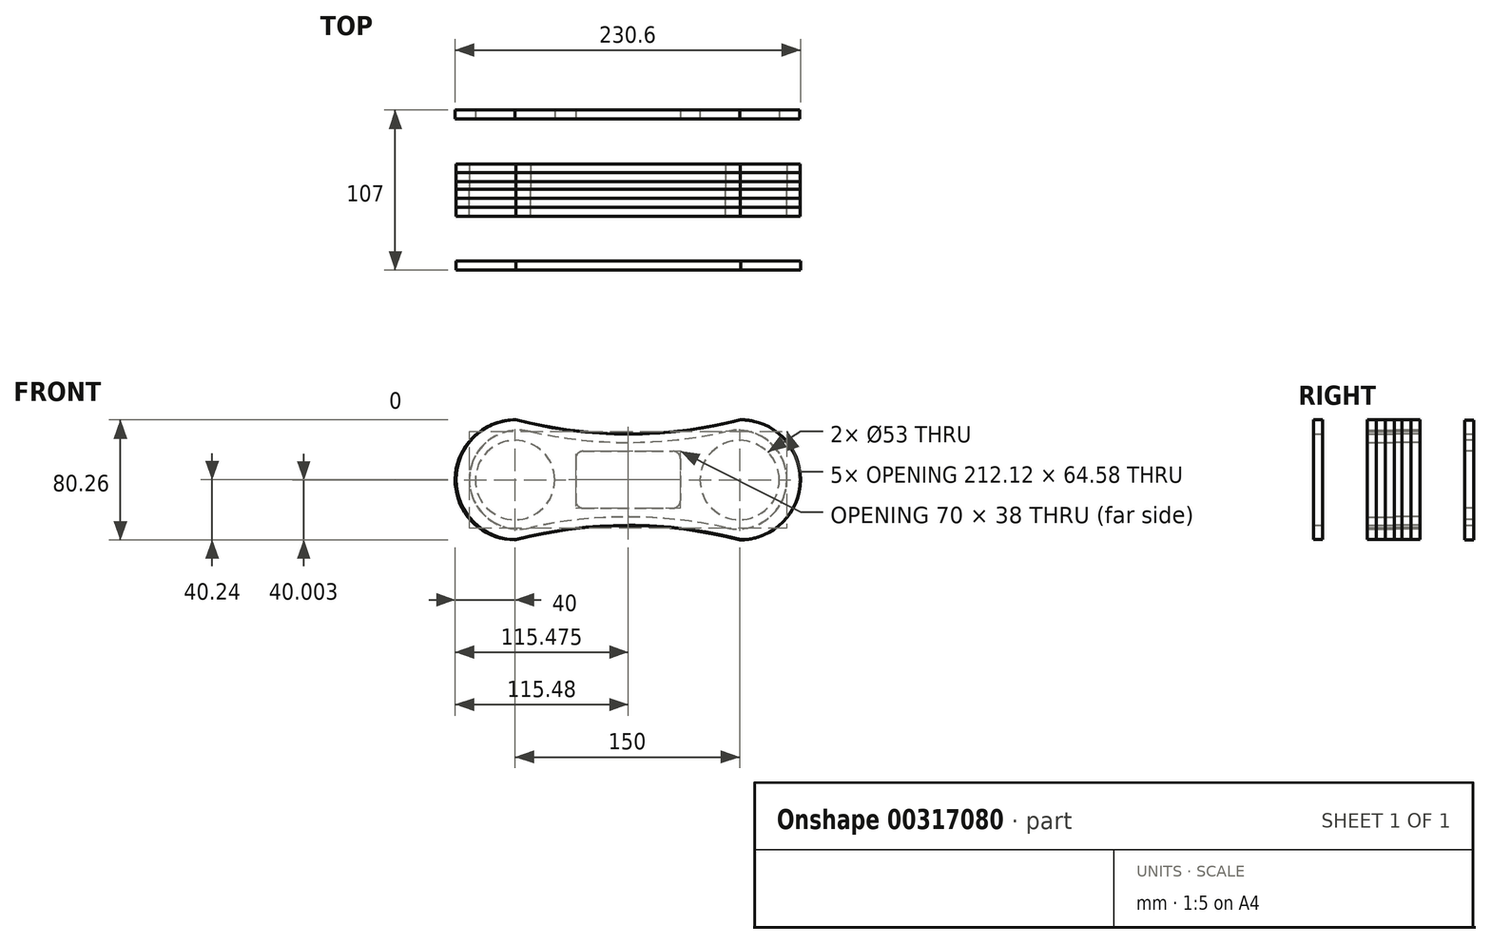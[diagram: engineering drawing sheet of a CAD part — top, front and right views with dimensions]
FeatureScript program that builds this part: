
annotation { "Feature Type Name" : "Feature", "Feature Type Description" : "" }
export const myFeature = defineFeature(function(context is Context, id is Id, definition is map)
    precondition{}
    {
        {
            var Q0;
            Q0=qCreatedBy(makeId("Front.planeOp"),FACE);
            var sketch = newSketch(context, id + "F0", { "sketchPlane" : qUnion([Q0])});
            skArc(sketch, "E0", {"start": v(75, -40) * mm, "mid": v(115, 0) * mm, "end": v(75, 40) * mm});
            skArc(sketch, "E1", {"start": v(-75, 40) * mm, "mid": v(-115, 0) * mm, "end": v(-75, -40) * mm});
            skArc(sketch, "E2", {"start": v(-75, 40) * mm, "mid": v(0, 30.47) * mm, "end": v(75, 40) * mm});
            skArc(sketch, "E3", {"start": v(75, -40) * mm, "mid": v(0, -30.47) * mm, "end": v(-75, -40) * mm});
            skPoint(sketch, "E4.middle", {"position": v(0, 0) * mm});
            skArc(sketch, "E5", {"start": v(-65, 32) * mm, "mid": v(0, 24.87) * mm, "end": v(65, 32) * mm});
            skArc(sketch, "E6", {"start": v(65, -32) * mm, "mid": v(0, -24.87) * mm, "end": v(-65, -32) * mm});
            skArc(sketch, "E7", {"start": v(-65, 32) * mm, "mid": v(-106.06, 0) * mm, "end": v(-65, -32) * mm});
            skArc(sketch, "E8", {"start": v(65, -32) * mm, "mid": v(106.06, 0) * mm, "end": v(65, 32) * mm});
            skSolve(sketch);
        }
        {
            var Q0;
            Q0=makeQuery(id+"F0.imprint","IMPRINT",FACE,{"disambiguationData":[TD([[makeQuery(id+"F0.imprint","IMPRINT",EDGE,{"derivedFrom":sQuery(id+"F0.wireOp",EDGE,"E0")}),1.0]])]});
            extrude(context, id + "F1", {"entities" : qUnion([Q0]), "depth" : 6 * mm});
        }
        {
            var Q0;
            Q0=qCreatedBy(makeId("Front.planeOp"),FACE);
            var sketch = newSketch(context, id + "F2", { "sketchPlane" : qUnion([Q0])});
            skArc(sketch, "E9", {"start": v(75.03, -39.98) * mm, "mid": v(115.03, 0.02) * mm, "end": v(75.03, 40.02) * mm});
            skArc(sketch, "E10", {"start": v(-74.97, 40.02) * mm, "mid": v(-114.97, 0.02) * mm, "end": v(-74.97, -39.98) * mm});
            skArc(sketch, "E11", {"start": v(-74.97, 40.02) * mm, "mid": v(0.03, 30.5) * mm, "end": v(75.03, 40.02) * mm});
            skArc(sketch, "E12", {"start": v(75.03, -39.98) * mm, "mid": v(0.03, -30.45) * mm, "end": v(-74.97, -39.98) * mm});
            skPoint(sketch, "E13.middle", {"position": v(0.03, 0.02) * mm});
            skArc(sketch, "E14", {"start": v(-64.97, 32.02) * mm, "mid": v(0.03, 24.9) * mm, "end": v(65.03, 32.02) * mm});
            skArc(sketch, "E15", {"start": v(65.03, -31.98) * mm, "mid": v(0.03, -24.85) * mm, "end": v(-64.97, -31.98) * mm});
            skArc(sketch, "E16", {"start": v(-64.97, 32.02) * mm, "mid": v(-106.04, 0.02) * mm, "end": v(-64.97, -31.98) * mm});
            skArc(sketch, "E17", {"start": v(65.03, -31.98) * mm, "mid": v(106.09, 0.02) * mm, "end": v(65.03, 32.02) * mm});
            skSolve(sketch);
        }
        {
            var Q0;
            Q0=qSketchRegion(id+"F2",true);
            extrude(context, id + "F3", {"entities" : qUnion([Q0]), "operationType" : NewBodyOperationType.ADD, "oppositeDirection" : true, "depth" : 5 * mm});
        }
        {
            var Q0;
            Q0=makeQuery(id+"F1.opExtrude","CAP_FACE",FACE,{"disambiguationData":[OSD([sQuery(id+"F0.wireOp",EDGE,"E0"),sQuery(id+"F0.wireOp",EDGE,"E1"),sQuery(id+"F0.wireOp",EDGE,"E2"),sQuery(id+"F0.wireOp",EDGE,"E3"),sQuery(id+"F0.wireOp",EDGE,"E5"),sQuery(id+"F0.wireOp",EDGE,"E6"),sQuery(id+"F0.wireOp",EDGE,"E7"),sQuery(id+"F0.wireOp",EDGE,"E8")])],"isStart":false});
            extrude(context, id + "F4", {"entities" : qUnion([Q0]), "depth" : 6 * mm});
        }
        {
            var Q0;
            Q0=makeQuery(id+"F3.opExtrude","CAP_FACE",FACE,{"disambiguationData":[OSD([sQuery(id+"F2.wireOp",EDGE,"E9"),sQuery(id+"F2.wireOp",EDGE,"E10"),sQuery(id+"F2.wireOp",EDGE,"E11"),sQuery(id+"F2.wireOp",EDGE,"E12"),sQuery(id+"F2.wireOp",EDGE,"E14"),sQuery(id+"F2.wireOp",EDGE,"E15"),sQuery(id+"F2.wireOp",EDGE,"E16"),sQuery(id+"F2.wireOp",EDGE,"E17")])],"isStart":false});
            extrude(context, id + "F5", {"entities" : qUnion([Q0]), "depth" : 6 * mm});
        }
        {
            var Q0;
            Q0=makeQuery(id+"F5.opExtrude","CAP_FACE",FACE,{"disambiguationData":[OSD([sQuery(id+"F2.wireOp",EDGE,"E9"),sQuery(id+"F2.wireOp",EDGE,"E10"),sQuery(id+"F2.wireOp",EDGE,"E11"),sQuery(id+"F2.wireOp",EDGE,"E12"),sQuery(id+"F2.wireOp",EDGE,"E14"),sQuery(id+"F2.wireOp",EDGE,"E15"),sQuery(id+"F2.wireOp",EDGE,"E16"),sQuery(id+"F2.wireOp",EDGE,"E17")])],"isStart":false});
            extrude(context, id + "F6", {"entities" : qUnion([Q0]), "depth" : 6 * mm});
        }
        {
            var Q0;
            Q0=makeQuery(id+"F4.opExtrude","CAP_FACE",FACE,{"disambiguationData":[OSD([sQuery(id+"F0.wireOp",EDGE,"E0"),sQuery(id+"F0.wireOp",EDGE,"E1"),sQuery(id+"F0.wireOp",EDGE,"E2"),sQuery(id+"F0.wireOp",EDGE,"E3"),sQuery(id+"F0.wireOp",EDGE,"E5"),sQuery(id+"F0.wireOp",EDGE,"E6"),sQuery(id+"F0.wireOp",EDGE,"E7"),sQuery(id+"F0.wireOp",EDGE,"E8")])],"isStart":false});
            extrude(context, id + "F7", {"entities" : qUnion([Q0]), "depth" : 6 * mm});
        }
        {
            var Q0;
            Q0=makeQuery(id+"F7.opExtrude","CAP_FACE",FACE,{"disambiguationData":[OSD([sQuery(id+"F0.wireOp",EDGE,"E0"),sQuery(id+"F0.wireOp",EDGE,"E1"),sQuery(id+"F0.wireOp",EDGE,"E2"),sQuery(id+"F0.wireOp",EDGE,"E3"),sQuery(id+"F0.wireOp",EDGE,"E5"),sQuery(id+"F0.wireOp",EDGE,"E6"),sQuery(id+"F0.wireOp",EDGE,"E7"),sQuery(id+"F0.wireOp",EDGE,"E8")])],"isStart":false});
            cPlane(context, id + "F8", {"entities" : qUnion([Q0]), "cplaneType" : CPlaneType.OFFSET, "offset" : 30 * mm, "width" : 150 * mm, "height" : 150 * mm});
        }
        {
            var Q0;
            Q0=qCreatedBy(id+"F8.planeOp",FACE);
            var sketch = newSketch(context, id + "F9", { "sketchPlane" : qUnion([Q0])});
            skArc(sketch, "E18", {"start": v(75.12, -40) * mm, "mid": v(115.12, 0) * mm, "end": v(75.12, 40) * mm});
            skArc(sketch, "E19", {"start": v(-74.88, 40) * mm, "mid": v(-114.88, 0) * mm, "end": v(-74.88, -40) * mm});
            skArc(sketch, "E20", {"start": v(-74.88, 40) * mm, "mid": v(0.12, 30.47) * mm, "end": v(75.12, 40) * mm});
            skArc(sketch, "E21", {"start": v(75.12, -40) * mm, "mid": v(0.12, -30.47) * mm, "end": v(-74.88, -40) * mm});
            skSolve(sketch);
        }
        {
            var Q0;
            Q0 = qSketchRegion(id + "F9", true);
            extrude(context, id + "F10", {"entities" : qUnion([Q0]), "operationType" : NewBodyOperationType.ADD, "depth" : 6 * mm});
        }
        {
            var Q0;
            Q0=makeQuery(id+"F6.opExtrude","CAP_FACE",FACE,{"disambiguationData":[OSD([sQuery(id+"F2.wireOp",EDGE,"E9"),sQuery(id+"F2.wireOp",EDGE,"E10"),sQuery(id+"F2.wireOp",EDGE,"E11"),sQuery(id+"F2.wireOp",EDGE,"E12"),sQuery(id+"F2.wireOp",EDGE,"E14"),sQuery(id+"F2.wireOp",EDGE,"E15"),sQuery(id+"F2.wireOp",EDGE,"E16"),sQuery(id+"F2.wireOp",EDGE,"E17")])],"isStart":false});
            cPlane(context, id + "F11", {"entities" : qUnion([Q0]), "cplaneType" : CPlaneType.OFFSET, "offset" : 30 * mm, "width" : 150 * mm, "height" : 150 * mm});
        }
        {
            var Q0;
            Q0=qCreatedBy(id+"F11.planeOp",FACE);
            var sketch = newSketch(context, id + "F12", { "sketchPlane" : qUnion([Q0])});
            skLineSegment(sketch, "E22.bottom", {"start": v(30, 19) * mm, "end": v(-30, 19) * mm});
            skLineSegment(sketch, "E22.top", {"start": v(30, -19) * mm, "end": v(-30, -19) * mm});
            skLineSegment(sketch, "E22.left", {"start": v(35, 14) * mm, "end": v(35, -14) * mm});
            skLineSegment(sketch, "E22.right", {"start": v(-35, 14) * mm, "end": v(-35, -14) * mm});
            skArc(sketch, "E23.filletArc", {"start": v(-30, 19) * mm, "mid": v(-33.53, 17.54) * mm, "end": v(-35, 14) * mm});
            skArc(sketch, "E24.filletArc", {"start": v(35, 14) * mm, "mid": v(33.54, 17.54) * mm, "end": v(30, 19) * mm});
            skArc(sketch, "E25.filletArc", {"start": v(30, -19) * mm, "mid": v(33.54, -17.54) * mm, "end": v(35, -14) * mm});
            skArc(sketch, "E26.filletArc", {"start": v(-35, -14) * mm, "mid": v(-33.53, -17.54) * mm, "end": v(-30, -19) * mm});
            skArc(sketch, "E27", {"start": v(75.48, -40.24) * mm, "mid": v(115.48, -0.24) * mm, "end": v(75.48, 39.76) * mm});
            skArc(sketch, "E28", {"start": v(-74.52, 39.76) * mm, "mid": v(-114.52, -0.24) * mm, "end": v(-74.52, -40.24) * mm});
            skArc(sketch, "E29", {"start": v(-74.52, 39.76) * mm, "mid": v(0.48, 30.24) * mm, "end": v(75.48, 39.76) * mm});
            skArc(sketch, "E30", {"start": v(75.48, -40.24) * mm, "mid": v(0.48, -30.71) * mm, "end": v(-74.52, -40.24) * mm});
            skCircle(sketch, "E31", {"center": v(-74.52, -0.24) * mm, "radius": 26.5 * mm});
            skCircle(sketch, "E32", {"center": v(75.48, -0.24) * mm, "radius": 26.5 * mm});
            skSolve(sketch);
        }
        {
            var Q0;
            Q0=makeQuery(id+"F12.imprint","IMPRINT",FACE,{"disambiguationData":[TD([[makeQuery(id+"F12.imprint","IMPRINT",EDGE,{"derivedFrom":sQuery(id+"F12.wireOp",EDGE,"E22.bottom")}),-1.0]])]});
            extrude(context, id + "F13", {"entities" : qUnion([Q0]), "operationType" : NewBodyOperationType.ADD, "depth" : 6 * mm});
        }
    });
